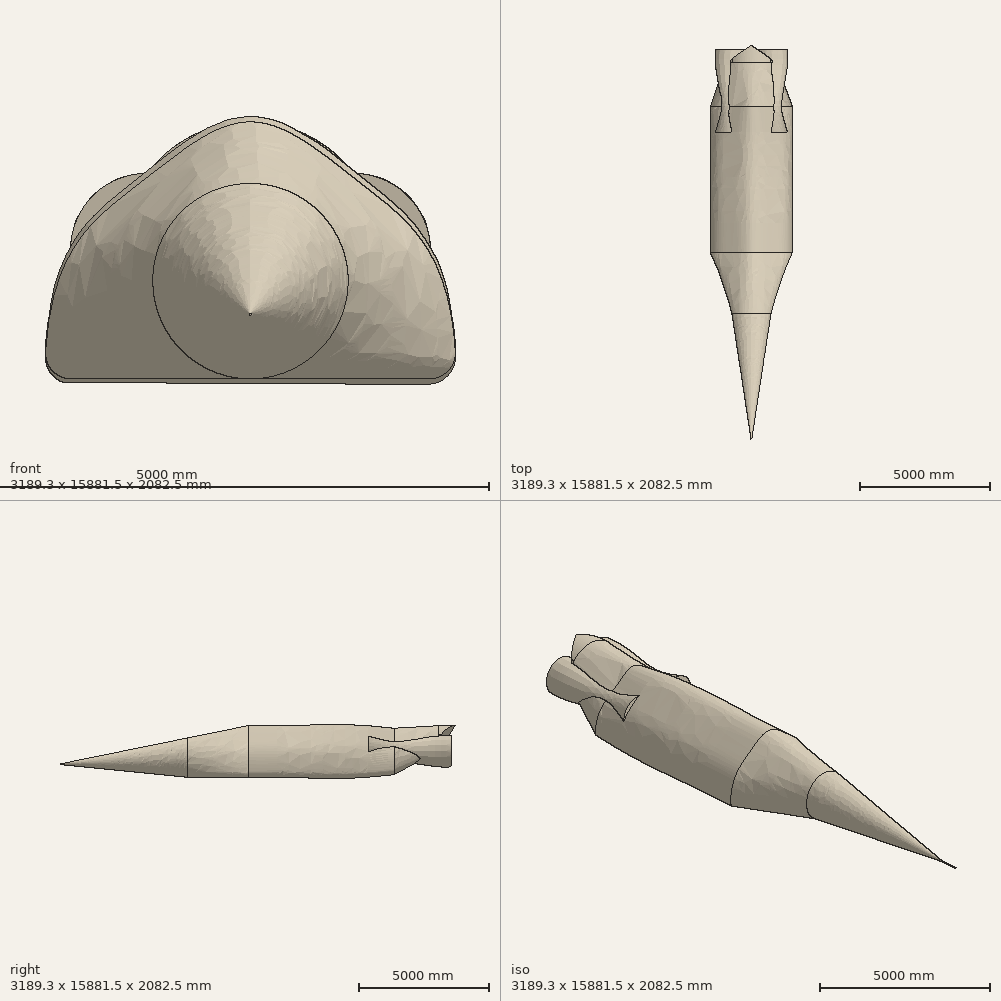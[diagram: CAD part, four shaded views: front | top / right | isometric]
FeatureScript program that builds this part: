
annotation { "Feature Type Name" : "Feature", "Feature Type Description" : "" }
export const myFeature = defineFeature(function(context is Context, id is Id, definition is map)
    precondition{}
    {
        {
            var Q0;
            Q0=qCreatedBy(makeId("Right.planeOp"),FACE);
            var sketch = newSketch(context, id + "F0", { "sketchPlane" : qUnion([Q0])});
            skLineSegment(sketch, "E0", {"start": v(0, 0) * mm, "end": v(-1750, 0) * mm});
            skLineSegment(sketch, "E1", {"start": v(-1750, 0) * mm, "end": v(-3500, 0) * mm});
            skLineSegment(sketch, "E2", {"start": v(-3500, 0) * mm, "end": v(-3500, -1000) * mm});
            skLineSegment(sketch, "E3", {"start": v(-3500, -1000) * mm, "end": v(-8500, -1000) * mm});
            skLineSegment(sketch, "E4", {"start": v(-8500, -1000) * mm, "end": v(-8500, -499.31) * mm});
            skLineSegment(sketch, "E5", {"start": v(-1151.4, 0) * mm, "end": v(-1151.4, 1000) * mm});
            skLineSegment(sketch, "E6", {"start": v(-1151.4, 1000) * mm, "end": v(-8500, -499.31) * mm});
            skLineSegment(sketch, "E7", {"start": v(-8500, -499.31) * mm, "end": v(-3500, -1000) * mm});
            skLineSegment(sketch, "E8", {"start": v(-3500, 0) * mm, "end": v(-3500, 520.82) * mm});
            skLineSegment(sketch, "E9", {"start": v(-8500, -499.31) * mm, "end": v(-8450, -499.31) * mm});
            skLineSegment(sketch, "E10", {"start": v(-8450, -499.31) * mm, "end": v(-8450, -489.1) * mm});
            skLineSegment(sketch, "E11", {"start": v(-8450, -499.31) * mm, "end": v(-8450, -504.32) * mm});
            skSolve(sketch);
        }
        {
            var Q0;
            Q0=sQuery(id+"F0.wireOp",EDGE,"E5");
            cPlane(context, id + "F1", {"entities" : qUnion([Q0]), "cplaneType" : CPlaneType.LINE_ANGLE, "offset" : 25 * mm, "angle" : 90 * degree, "oppositeDirection" : true, "width" : 150 * mm, "height" : 150 * mm});
        }
        {
            var Q0;
            Q0=qCreatedBy(id+"F1.planeOp",FACE);
            var sketch = newSketch(context, id + "F2", { "sketchPlane" : qUnion([Q0])});
            skLineSegment(sketch, "E12.top", {"start": v(-1394.2, -1000) * mm, "end": v(1394.2, -1000) * mm});
            skPoint(sketch, "E12.middle", {"position": v(0, 0) * mm});
            skFitSpline(sketch, "E13", {"points": [v(-1600, -1000) * mm, v(-848, 530) * mm, v(0, 1000) * mm, v(848, 530) * mm, v(1600, -1000) * mm], "startDerivative": vector(0, 10524.75) * mm, "endDerivative": vector(0, -10524.75) * mm});
            skArc(sketch, "E14", {"start": v(-735.27, 618.52) * mm, "mid": v(-1273.27, 435.52) * mm, "end": v(-1440.68, -107.53) * mm});
            skArc(sketch, "E15", {"start": v(1440.68, -107.53) * mm, "mid": v(1273.27, 435.52) * mm, "end": v(735.27, 618.52) * mm});
            skFitSpline(sketch, "E16.trimOffspring", {"points": [v(-1600, -1000) * mm, v(-848, 530) * mm, v(0, 1000) * mm, v(848, 530) * mm, v(1600, -1000) * mm], "startDerivative": vector(0, 10524.75) * mm, "endDerivative": vector(0, -10524.75) * mm});
            skFitSpline(sketch, "E17.trimOffspring", {"points": [v(-1600, -1000) * mm, v(-848, 530) * mm, v(0, 1000) * mm, v(848, 530) * mm, v(1600, -1000) * mm], "startDerivative": vector(0, 10524.75) * mm, "endDerivative": vector(0, -10524.75) * mm});
            skArc(sketch, "E18.filletArc", {"start": v(-1593.82, -787.83) * mm, "mid": v(-1539.85, -937.05) * mm, "end": v(-1394.2, -1000) * mm});
            skArc(sketch, "E19.filletArc", {"start": v(1394.2, -1000) * mm, "mid": v(1539.85, -937.05) * mm, "end": v(1593.82, -787.83) * mm});
            skSolve(sketch);
        }
        {
            var Q0;
            Q0=qCreatedBy(makeId("Front.planeOp"),FACE);
            var sketch = newSketch(context, id + "F3", { "sketchPlane" : qUnion([Q0])});
            skLineSegment(sketch, "E20.top", {"start": v(-1394.2, -1000) * mm, "end": v(1394.2, -1000) * mm});
            skPoint(sketch, "E20.middle", {"position": v(0, 0) * mm});
            skFitSpline(sketch, "E21", {"points": [v(-1600, -1000) * mm, v(-848, 530) * mm, v(0, 1000) * mm, v(848, 530) * mm, v(1600, -1000) * mm], "startDerivative": vector(0, 10524.75) * mm, "endDerivative": vector(0, -10524.75) * mm});
            skArc(sketch, "E22", {"start": v(-735.27, 618.52) * mm, "mid": v(-1273.27, 435.52) * mm, "end": v(-1440.68, -107.53) * mm});
            skArc(sketch, "E23", {"start": v(1440.68, -107.53) * mm, "mid": v(1273.27, 435.52) * mm, "end": v(735.27, 618.52) * mm});
            skFitSpline(sketch, "E24.trimOffspring", {"points": [v(-1600, -1000) * mm, v(-848, 530) * mm, v(0, 1000) * mm, v(848, 530) * mm, v(1600, -1000) * mm], "startDerivative": vector(0, 10524.75) * mm, "endDerivative": vector(0, -10524.75) * mm});
            skFitSpline(sketch, "E25.trimOffspring", {"points": [v(-1600, -1000) * mm, v(-848, 530) * mm, v(0, 1000) * mm, v(848, 530) * mm, v(1600, -1000) * mm], "startDerivative": vector(0, 10524.75) * mm, "endDerivative": vector(0, -10524.75) * mm});
            skArc(sketch, "E26.filletArc", {"start": v(-1593.82, -787.83) * mm, "mid": v(-1539.85, -937.05) * mm, "end": v(-1394.2, -1000) * mm});
            skArc(sketch, "E27.filletArc", {"start": v(1394.2, -1000) * mm, "mid": v(1539.85, -937.05) * mm, "end": v(1593.82, -787.83) * mm});
            skSolve(sketch);
        }
        {
            var Q0;
            Q0=qCreatedBy(makeId("Front.planeOp"),FACE);
            cPlane(context, id + "F4", {"entities" : qUnion([Q0]), "cplaneType" : CPlaneType.OFFSET, "offset" : 3500 * mm, "oppositeDirection" : true, "width" : 150 * mm, "height" : 150 * mm});
        }
        {
            var Q0;
            Q0=qCreatedBy(id+"F4.planeOp",FACE);
            var sketch = newSketch(context, id + "F5", { "sketchPlane" : qUnion([Q0])});
            skLineSegment(sketch, "E28.top", {"start": v(-1394.2, -1000) * mm, "end": v(1394.2, -1000) * mm});
            skPoint(sketch, "E28.middle", {"position": v(0, 0) * mm});
            skFitSpline(sketch, "E29", {"points": [v(-1600, -1000) * mm, v(-848, 530) * mm, v(0, 1000) * mm, v(848, 530) * mm, v(1600, -1000) * mm], "startDerivative": vector(0, 10524.75) * mm, "endDerivative": vector(0, -10524.75) * mm});
            skArc(sketch, "E30", {"start": v(-735.27, 618.52) * mm, "mid": v(-1273.27, 435.52) * mm, "end": v(-1440.68, -107.53) * mm});
            skArc(sketch, "E31", {"start": v(1440.68, -107.53) * mm, "mid": v(1273.27, 435.52) * mm, "end": v(735.27, 618.52) * mm});
            skFitSpline(sketch, "E32.trimOffspring", {"points": [v(-1600, -1000) * mm, v(-848, 530) * mm, v(0, 1000) * mm, v(848, 530) * mm, v(1600, -1000) * mm], "startDerivative": vector(0, 10524.75) * mm, "endDerivative": vector(0, -10524.75) * mm});
            skFitSpline(sketch, "E33.trimOffspring", {"points": [v(-1600, -1000) * mm, v(-848, 530) * mm, v(0, 1000) * mm, v(848, 530) * mm, v(1600, -1000) * mm], "startDerivative": vector(0, 10524.75) * mm, "endDerivative": vector(0, -10524.75) * mm});
            skArc(sketch, "E34.filletArc", {"start": v(-1593.82, -787.83) * mm, "mid": v(-1539.85, -937.05) * mm, "end": v(-1394.2, -1000) * mm});
            skArc(sketch, "E35.filletArc", {"start": v(1394.2, -1000) * mm, "mid": v(1539.85, -937.05) * mm, "end": v(1593.82, -787.83) * mm});
            skSolve(sketch);
        }
        {
            var Q0;
            Q0=qCreatedBy(makeId("Front.planeOp"),FACE);
            cPlane(context, id + "F6", {"entities" : qUnion([Q0]), "cplaneType" : CPlaneType.OFFSET, "offset" : 4500 * mm, "oppositeDirection" : true, "width" : 150 * mm, "height" : 150 * mm});
        }
        {
            var Q0;
            Q0=qCreatedBy(id+"F6.planeOp",FACE);
            var sketch = newSketch(context, id + "F7", { "sketchPlane" : qUnion([Q0])});
            skLineSegment(sketch, "E36.top", {"start": v(-1413.07, -900) * mm, "end": v(1413.07, -900) * mm});
            skPoint(sketch, "E36.middle", {"position": v(0, 0) * mm});
            skFitSpline(sketch, "E37", {"points": [v(-1600, -900) * mm, v(-784.42, 441.24) * mm, v(0, 900) * mm, v(784.42, 441.24) * mm, v(1600, -900) * mm], "startDerivative": vector(0, 9508.62) * mm, "endDerivative": vector(0, -9508.62) * mm});
            skArc(sketch, "E38", {"start": v(-719.25, 488.69) * mm, "mid": v(-1131.76, 394.84) * mm, "end": v(-1324.66, 18.33) * mm});
            skArc(sketch, "E39", {"start": v(1324.66, 18.33) * mm, "mid": v(1131.76, 394.84) * mm, "end": v(719.25, 488.69) * mm});
            skFitSpline(sketch, "E40.trimOffspring", {"points": [v(-1600, -900) * mm, v(-784.42, 441.24) * mm, v(0, 900) * mm, v(784.42, 441.24) * mm, v(1600, -900) * mm], "startDerivative": vector(0, 9508.62) * mm, "endDerivative": vector(0, -9508.62) * mm});
            skFitSpline(sketch, "E41.trimOffspring", {"points": [v(-1600, -900) * mm, v(-784.42, 441.24) * mm, v(0, 900) * mm, v(784.42, 441.24) * mm, v(1600, -900) * mm], "startDerivative": vector(0, 9508.62) * mm, "endDerivative": vector(0, -9508.62) * mm});
            skArc(sketch, "E42.filletArc", {"start": v(-1592.48, -705.43) * mm, "mid": v(-1545.4, -842.02) * mm, "end": v(-1413.07, -900) * mm});
            skArc(sketch, "E43.filletArc", {"start": v(1413.07, -900) * mm, "mid": v(1545.4, -842.02) * mm, "end": v(1592.48, -705.43) * mm});
            skLineSegment(sketch, "E44", {"start": v(-719.25, 488.69) * mm, "end": v(-1324.66, 18.33) * mm, "construction": true});
            skLineSegment(sketch, "E45", {"start": v(719.25, 488.69) * mm, "end": v(1324.66, 18.33) * mm, "construction": true});
            skSolve(sketch);
        }
        {
            var Q0;
            Q0=qCreatedBy(makeId("Front.planeOp"),FACE);
            cPlane(context, id + "F8", {"entities" : qUnion([Q0]), "cplaneType" : CPlaneType.OFFSET, "offset" : 6232.05 * mm, "oppositeDirection" : true, "width" : 150 * mm, "height" : 150 * mm});
        }
        {
            var Q0;
            Q0=qCreatedBy(id+"F8.planeOp",FACE);
            var sketch = newSketch(context, id + "F9", { "sketchPlane" : qUnion([Q0])});
            skArc(sketch, "E46", {"start": v(998.61, 52.63) * mm, "mid": v(0, 1000) * mm, "end": v(-998.61, 52.63) * mm});
            skLineSegment(sketch, "E47", {"start": v(0, 0) * mm, "end": v(-948.68, 0) * mm});
            skLineSegment(sketch, "E48", {"start": v(0, 0) * mm, "end": v(948.68, 0) * mm});
            skLineSegment(sketch, "E49", {"start": v(0, 1000) * mm, "end": v(0, 675) * mm, "construction": true});
            skLineSegment(sketch, "E50", {"start": v(0, 675) * mm, "end": v(-737.82, 675) * mm, "construction": true});
            skLineSegment(sketch, "E51", {"start": v(0, 675) * mm, "end": v(737.82, 675) * mm, "construction": true});
            skPoint(sketch, "E52.visualSharp", {"position": v(-1000, 0) * mm});
            skArc(sketch, "E52.filletArc", {"start": v(-998.61, 52.63) * mm, "mid": v(-984.96, 15.59) * mm, "end": v(-948.68, 0) * mm});
            skPoint(sketch, "E53.visualSharp", {"position": v(1000, 0) * mm});
            skArc(sketch, "E53.filletArc", {"start": v(948.68, 0) * mm, "mid": v(984.96, 15.59) * mm, "end": v(998.61, 52.63) * mm});
            skSolve(sketch);
        }
        {
            var Q0;
            Q0=makeQuery(id+"F2.imprint","IMPRINT",FACE,{"disambiguationData":[TD([[makeQuery(id+"F2.imprint","IMPRINT",EDGE,{"derivedFrom":sQuery(id+"F2.wireOp",EDGE,"E12.top")}),1.0]])]});
            var Q1;
            Q1=makeQuery(id+"F3.imprint","IMPRINT",FACE,{"disambiguationData":[TD([[makeQuery(id+"F3.imprint","IMPRINT",EDGE,{"derivedFrom":sQuery(id+"F3.wireOp",EDGE,"E20.top")}),1.0]])]});
            var Q2;
            Q2=makeQuery(id+"F5.imprint","IMPRINT",FACE,{"disambiguationData":[TD([[makeQuery(id+"F5.imprint","IMPRINT",EDGE,{"derivedFrom":sQuery(id+"F5.wireOp",EDGE,"E28.top")}),1.0]])]});
            var Q3;
            Q3=makeQuery(id+"F7.imprint","IMPRINT",FACE,{"disambiguationData":[TD([[makeQuery(id+"F7.imprint","IMPRINT",EDGE,{"derivedFrom":sQuery(id+"F7.wireOp",EDGE,"E36.top")}),1.0]])]});
            loft(context, id + "F10", {"sheetProfilesArray" : [{ "sheetProfileEntities" : qUnion([Q0]) }, { "sheetProfileEntities" : qUnion([Q1]) }, { "sheetProfileEntities" : qUnion([Q2]) }, { "sheetProfileEntities" : qUnion([Q3]) }]});
        }
        {
            var Q0;
            Q0=sQuery(id+"F7.wireOp",EDGE,"E44");
            var Q1;
            Q1=sQuery(id+"F9.wireOp",VERTEX,"E50.end");
            cPlane(context, id + "F11", {"entities" : qUnion([Q0, Q1]), "cplaneType" : CPlaneType.LINE_ANGLE, "offset" : 25 * mm, "angle" : 180 * degree, "width" : 150 * mm, "height" : 150 * mm});
        }
        {
            var Q0;
            Q0=qCreatedBy(id+"F11.planeOp",FACE);
            var sketch = newSketch(context, id + "F12", { "sketchPlane" : qUnion([Q0])});
            skLineSegment(sketch, "E54", {"start": v(-589.34, 4526.34) * mm, "end": v(-612.8, 6268.32) * mm});
            skLineSegment(sketch, "E55", {"start": v(-1354.08, 4472.19) * mm, "end": v(-612.8, 6268.32) * mm});
            skSolve(sketch);
        }
        {
            var Q0;
            Q0=sQuery(id+"F7.wireOp",EDGE,"E45");
            var Q1;
            Q1=sQuery(id+"F9.wireOp",VERTEX,"E51.end");
            cPlane(context, id + "F13", {"entities" : qUnion([Q0, Q1]), "cplaneType" : CPlaneType.LINE_ANGLE, "offset" : 25 * mm, "angle" : 0 * degree, "width" : 150 * mm, "height" : 150 * mm});
        }
        {
            var Q0;
            Q0=qCreatedBy(id+"F13.planeOp",FACE);
            var sketch = newSketch(context, id + "F14", { "sketchPlane" : qUnion([Q0])});
            skLineSegment(sketch, "E56", {"start": v(589.34, 4526.34) * mm, "end": v(612.8, 6268.32) * mm});
            skLineSegment(sketch, "E57", {"start": v(1354.08, 4472.19) * mm, "end": v(612.8, 6268.32) * mm});
            skSolve(sketch);
        }
        {
            var Q1;
            Q1=makeQuery(id+"F10.opLoft","CAP_FACE",FACE,{"disambiguationData":[OSD([makeQuery(id+"F7.imprint","IMPRINT",FACE,{"disambiguationData":[TD([[makeQuery(id+"F7.imprint","IMPRINT",EDGE,{"derivedFrom":sQuery(id+"F7.wireOp",EDGE,"E36.top")}),1.0]])]})])],"isStart":true});
            var Q2;
            Q2=makeQuery(id+"F9.imprint","IMPRINT",FACE,{"disambiguationData":[TD([[makeQuery(id+"F9.imprint","IMPRINT",EDGE,{"derivedFrom":sQuery(id+"F9.wireOp",EDGE,"E46")}),1.0]])]});
            var Q3;
            Q3=sQuery(id+"F12.wireOp",EDGE,"E54");
            var Q4;
            Q4=sQuery(id+"F14.wireOp",EDGE,"E56");
            loft(context, id + "F15", {"operationType" : NewBodyOperationType.ADD, "addGuides" : true, "sheetProfilesArray" : [{ "sheetProfileEntities" : qUnion([Q1]) }, { "sheetProfileEntities" : qUnion([Q2]) }], "guidesArray" : [{ "guideEntities" : qUnion([Q3]), "guideDerivativeType" : LoftGuideDerivativeType.DEFAULT, "guideDerivativeMagnitude" : 1 }, { "guideEntities" : qUnion([Q4]), "guideDerivativeType" : LoftGuideDerivativeType.DEFAULT, "guideDerivativeMagnitude" : 1 }]});
        }
        {
            var Q0;
            Q0=makeQuery(id+"F15.opLoft","CAP_FACE",FACE,{"disambiguationData":[OSD([makeQuery(id+"F9.imprint","IMPRINT",FACE,{"disambiguationData":[TD([[makeQuery(id+"F9.imprint","IMPRINT",EDGE,{"derivedFrom":sQuery(id+"F9.wireOp",EDGE,"E46")}),1.0]])]})])],"isStart":true});
            extrude(context, id + "F16", {"entities" : qUnion([Q0]), "operationType" : NewBodyOperationType.ADD, "depth" : 649.4 * mm, "offsetDistance" : 25 * mm});
        }
        {
            var Q0;
            Q0=qCreatedBy(makeId("Right.planeOp"),FACE);
            var sketch = newSketch(context, id + "F17", { "sketchPlane" : qUnion([Q0])});
            skLineSegment(sketch, "E58", {"start": v(0, 0) * mm, "end": v(4500, 0) * mm});
            skLineSegment(sketch, "E59", {"start": v(4500, 0) * mm, "end": v(6232.05, 0) * mm});
            skLineSegment(sketch, "E60", {"start": v(4500, 0) * mm, "end": v(4500, 1000) * mm});
            skLineSegment(sketch, "E61", {"start": v(4500, 1000) * mm, "end": v(6881.46, 1000) * mm});
            skLineSegment(sketch, "E62", {"start": v(6881.46, 1000) * mm, "end": v(6881.46, -1000) * mm});
            skLineSegment(sketch, "E63", {"start": v(6881.46, 1000) * mm, "end": v(6232.05, 0) * mm});
            skLineSegment(sketch, "E64", {"start": v(6232.05, 0) * mm, "end": v(5582.64, -1000) * mm});
            skLineSegment(sketch, "E65", {"start": v(5582.64, -1000) * mm, "end": v(6881.46, -1000) * mm});
            skSolve(sketch);
        }
        {
            var Q0;
            Q0=makeQuery(id+"F17.imprint","IMPRINT",FACE,{"disambiguationData":[TD([[makeQuery(id+"F17.imprint","IMPRINT",EDGE,{"derivedFrom":sQuery(id+"F17.wireOp",EDGE,"E62")}),-1.0]])]});
            var Q1;
            Q1=sQuery(id+"F17.wireOp",EDGE,"E61");
            revolve(context, id + "F18", {"operationType" : NewBodyOperationType.REMOVE, "entities" : qUnion([Q0]), "axis" : qUnion([Q1]), "revolveType" : RevolveType.SYMMETRIC, "oppositeDirection" : true, "angle" : 182 * degree});
        }
        {
            var Q0;
            Q0=qCreatedBy(id+"F1.planeOp",FACE);
            var sketch = newSketch(context, id + "F19", { "sketchPlane" : qUnion([Q0])});
            skLineSegment(sketch, "E66.top", {"start": v(-1394.2, -1000) * mm, "end": v(1394.2, -1000) * mm});
            skPoint(sketch, "E66.middle", {"position": v(0, 0) * mm});
            skFitSpline(sketch, "E67", {"points": [v(-1600, -1000) * mm, v(-848, 530) * mm, v(0, 1000) * mm, v(848, 530) * mm, v(1600, -1000) * mm], "startDerivative": vector(0, 10524.75) * mm, "endDerivative": vector(0, -10524.75) * mm});
            skArc(sketch, "E68.filletArc", {"start": v(-1593.82, -787.83) * mm, "mid": v(-1539.85, -937.05) * mm, "end": v(-1394.2, -1000) * mm});
            skArc(sketch, "E69.filletArc", {"start": v(1394.2, -1000) * mm, "mid": v(1539.85, -937.05) * mm, "end": v(1593.82, -787.83) * mm});
            skLineSegment(sketch, "E70", {"start": v(-1593.82, -787.83) * mm, "end": v(-1394.2, -1000) * mm, "construction": true});
            skLineSegment(sketch, "E71", {"start": v(1593.82, -787.83) * mm, "end": v(1394.2, -1000) * mm, "construction": true});
            skSolve(sketch);
        }
        {
            var Q0;
            Q0=qCreatedBy(makeId("Front.planeOp"),FACE);
            cPlane(context, id + "F20", {"entities" : qUnion([Q0]), "cplaneType" : CPlaneType.OFFSET, "offset" : 3500 * mm, "width" : 150 * mm, "height" : 150 * mm});
        }
        {
            var Q0;
            Q0=qCreatedBy(id+"F20.planeOp",FACE);
            var sketch = newSketch(context, id + "F21", { "sketchPlane" : qUnion([Q0])});
            skCircle(sketch, "E72", {"center": v(0, -239.59) * mm, "radius": 760.41 * mm});
            skLineSegment(sketch, "E73", {"start": v(0, -1000) * mm, "end": v(0, -800) * mm, "construction": true});
            skLineSegment(sketch, "E74", {"start": v(0, -800) * mm, "end": v(-513.97, -800) * mm, "construction": true});
            skLineSegment(sketch, "E75", {"start": v(0, -800) * mm, "end": v(513.97, -800) * mm, "construction": true});
            skSolve(sketch);
        }
        {
            var Q0;
            Q0=qCreatedBy(makeId("Front.planeOp"),FACE);
            cPlane(context, id + "F22", {"entities" : qUnion([Q0]), "cplaneType" : CPlaneType.OFFSET, "offset" : 8450 * mm, "width" : 150 * mm, "height" : 150 * mm});
        }
        {
            var Q0;
            Q0=qCreatedBy(id+"F22.planeOp",FACE);
            var sketch = newSketch(context, id + "F23", { "sketchPlane" : qUnion([Q0])});
            skCircle(sketch, "E76", {"center": v(0, -496.71) * mm, "radius": 7.6 * mm});
            skSolve(sketch);
        }
        {
            var Q0;
            Q0=sQuery(id+"F19.wireOp",EDGE,"E70");
            var Q1;
            Q1=sQuery(id+"F21.wireOp",VERTEX,"E74.end");
            cPlane(context, id + "F24", {"entities" : qUnion([Q0, Q1]), "cplaneType" : CPlaneType.LINE_ANGLE, "offset" : 25 * mm, "angle" : 0 * degree, "width" : 150 * mm, "height" : 150 * mm});
        }
        {
            var Q0;
            Q0=qCreatedBy(id+"F24.planeOp",FACE);
            var sketch = newSketch(context, id + "F25", { "sketchPlane" : qUnion([Q0])});
            skLineSegment(sketch, "E77", {"start": v(3032.27, -230.44) * mm, "end": v(558.11, 518.4) * mm});
            skLineSegment(sketch, "E78", {"start": v(3032.27, -230.44) * mm, "end": v(558.11, 227.09) * mm});
            skSolve(sketch);
        }
        {
            var Q0;
            Q0=sQuery(id+"F19.wireOp",EDGE,"E71");
            var Q1;
            Q1=sQuery(id+"F21.wireOp",VERTEX,"E75.end");
            cPlane(context, id + "F26", {"entities" : qUnion([Q0, Q1]), "cplaneType" : CPlaneType.LINE_ANGLE, "offset" : 25 * mm, "angle" : 180 * degree, "width" : 150 * mm, "height" : 150 * mm});
        }
        {
            var Q0;
            Q0=qCreatedBy(id+"F26.planeOp",FACE);
            var sketch = newSketch(context, id + "F27", { "sketchPlane" : qUnion([Q0])});
            skLineSegment(sketch, "E79", {"start": v(-3032.27, -230.44) * mm, "end": v(-558.11, 518.4) * mm});
            skLineSegment(sketch, "E80", {"start": v(-3032.27, -230.44) * mm, "end": v(-558.11, 227.09) * mm});
            skSolve(sketch);
        }
        {
            var Q1;
            Q1=makeQuery(id+"F19.imprint","IMPRINT",FACE,{"disambiguationData":[TD([[makeQuery(id+"F19.imprint","IMPRINT",EDGE,{"derivedFrom":sQuery(id+"F19.wireOp",EDGE,"E66.top")}),1.0]])]});
            var Q2;
            Q2=makeQuery(id+"F21.imprint","IMPRINT",FACE,{"disambiguationData":[TD([[makeQuery(id+"F21.imprint","IMPRINT",EDGE,{"derivedFrom":sQuery(id+"F21.wireOp",EDGE,"E72")}),1.0]])]});
            var Q3;
            Q3=sQuery(id+"F25.wireOp",EDGE,"E77");
            var Q4;
            Q4=sQuery(id+"F27.wireOp",EDGE,"E79");
            loft(context, id + "F28", {"operationType" : NewBodyOperationType.ADD, "addGuides" : true, "sheetProfilesArray" : [{ "sheetProfileEntities" : qUnion([Q1]) }, { "sheetProfileEntities" : qUnion([Q2]) }], "guidesArray" : [{ "guideEntities" : qUnion([Q3]), "guideDerivativeType" : LoftGuideDerivativeType.DEFAULT, "guideDerivativeMagnitude" : 1 }, { "guideEntities" : qUnion([Q4]), "guideDerivativeType" : LoftGuideDerivativeType.DEFAULT, "guideDerivativeMagnitude" : 1 }]});
        }
        {
            var Q1;
            Q1=makeQuery(id+"F28.opLoft","CAP_FACE",FACE,{"disambiguationData":[OSD([makeQuery(id+"F21.imprint","IMPRINT",FACE,{"disambiguationData":[TD([[makeQuery(id+"F21.imprint","IMPRINT",EDGE,{"derivedFrom":sQuery(id+"F21.wireOp",EDGE,"E72")}),1.0]])]})])],"isStart":true});
            var Q2;
            Q2=makeQuery(id+"F23.imprint","IMPRINT",FACE,{"disambiguationData":[TD([[makeQuery(id+"F23.imprint","IMPRINT",EDGE,{"derivedFrom":sQuery(id+"F23.wireOp",EDGE,"E76")}),1.0]])]});
            loft(context, id + "F29", {"operationType" : NewBodyOperationType.ADD, "sheetProfilesArray" : [{ "sheetProfileEntities" : qUnion([Q1]) }, { "sheetProfileEntities" : qUnion([Q2]) }]});
        }
        {
            var Q0;
            Q0=makeQuery(id+"F29.opLoft","CAP_FACE",FACE,{"disambiguationData":[OSD([makeQuery(id+"F23.imprint","IMPRINT",FACE,{"disambiguationData":[TD([[makeQuery(id+"F23.imprint","IMPRINT",EDGE,{"derivedFrom":sQuery(id+"F23.wireOp",EDGE,"E76")}),1.0]])]})])],"isStart":true});
            extrude(context, id + "F30", {"entities" : qUnion([Q0]), "operationType" : NewBodyOperationType.ADD, "depth" : 550 * mm, "offsetDistance" : 25 * mm});
        }
        {
            var Q0;
            Q0=qCreatedBy(makeId("Front.planeOp"),FACE);
            cPlane(context, id + "F31", {"entities" : qUnion([Q0]), "cplaneType" : CPlaneType.OFFSET, "offset" : 3500 * mm, "oppositeDirection" : true, "width" : 150 * mm, "height" : 150 * mm});
        }
        {
            var Q0;
            Q0=qCreatedBy(id+"F31.planeOp",FACE);
            var sketch = newSketch(context, id + "F32", { "sketchPlane" : qUnion([Q0])});
            skCircle(sketch, "E81", {"center": v(-800, 0) * mm, "radius": 600 * mm});
            skCircle(sketch, "E82", {"center": v(800, 0) * mm, "radius": 600 * mm});
            skSolve(sketch);
        }
        {
            var Q0;
            Q0=qCreatedBy(makeId("Front.planeOp"),FACE);
            cPlane(context, id + "F33", {"entities" : qUnion([Q0]), "cplaneType" : CPlaneType.OFFSET, "offset" : 4500 * mm, "oppositeDirection" : true, "width" : 150 * mm, "height" : 150 * mm});
        }
        {
            var Q0;
            Q0=qCreatedBy(id+"F33.planeOp",FACE);
            var sketch = newSketch(context, id + "F34", { "sketchPlane" : qUnion([Q0])});
            skCircle(sketch, "E83", {"center": v(-800, 0) * mm, "radius": 400 * mm});
            skCircle(sketch, "E84", {"center": v(800, 0) * mm, "radius": 400 * mm});
            skSolve(sketch);
        }
        {
            var Q0;
            Q0=qCreatedBy(makeId("Front.planeOp"),FACE);
            cPlane(context, id + "F35", {"entities" : qUnion([Q0]), "cplaneType" : CPlaneType.OFFSET, "offset" : 6232.05 * mm, "oppositeDirection" : true, "width" : 150 * mm, "height" : 150 * mm});
        }
        {
            var Q0;
            Q0=qCreatedBy(id+"F35.planeOp",FACE);
            var sketch = newSketch(context, id + "F36", { "sketchPlane" : qUnion([Q0])});
            skCircle(sketch, "E85", {"center": v(-800, 0) * mm, "radius": 600 * mm});
            skCircle(sketch, "E86", {"center": v(800, 0) * mm, "radius": 600 * mm});
            skSolve(sketch);
        }
        {
            var Q0;
            Q0=qCreatedBy(makeId("Front.planeOp"),FACE);
            cPlane(context, id + "F37", {"entities" : qUnion([Q0]), "cplaneType" : CPlaneType.OFFSET, "offset" : 6732.05 * mm, "oppositeDirection" : true, "width" : 150 * mm, "height" : 150 * mm});
        }
        {
            var Q0;
            Q0=qCreatedBy(id+"F37.planeOp",FACE);
            var sketch = newSketch(context, id + "F38", { "sketchPlane" : qUnion([Q0])});
            skCircle(sketch, "E87", {"center": v(-800, 0) * mm, "radius": 600 * mm});
            skCircle(sketch, "E88", {"center": v(800, 0) * mm, "radius": 600 * mm});
            skSolve(sketch);
        }
        {
            var Q0;
            Q0=makeQuery(id+"F32.imprint","IMPRINT",FACE,{"disambiguationData":[TD([[makeQuery(id+"F32.imprint","IMPRINT",EDGE,{"derivedFrom":sQuery(id+"F32.wireOp",EDGE,"E81")}),1.0]])]});
            var Q1;
            Q1=makeQuery(id+"F34.imprint","IMPRINT",FACE,{"disambiguationData":[TD([[makeQuery(id+"F34.imprint","IMPRINT",EDGE,{"derivedFrom":sQuery(id+"F34.wireOp",EDGE,"E83")}),1.0]])]});
            var Q2;
            Q2=makeQuery(id+"F36.imprint","IMPRINT",FACE,{"disambiguationData":[TD([[makeQuery(id+"F36.imprint","IMPRINT",EDGE,{"derivedFrom":sQuery(id+"F36.wireOp",EDGE,"E85")}),1.0]])]});
            var Q3;
            Q3=makeQuery(id+"F38.imprint","IMPRINT",FACE,{"disambiguationData":[TD([[makeQuery(id+"F38.imprint","IMPRINT",EDGE,{"derivedFrom":sQuery(id+"F38.wireOp",EDGE,"E87")}),1.0]])]});
            loft(context, id + "F39", {"sheetProfilesArray" : [{ "sheetProfileEntities" : qUnion([Q0]) }, { "sheetProfileEntities" : qUnion([Q1]) }, { "sheetProfileEntities" : qUnion([Q2]) }, { "sheetProfileEntities" : qUnion([Q3]) }]});
        }
        {
            var Q0;
            Q0=makeQuery(id+"F32.imprint","IMPRINT",FACE,{"disambiguationData":[TD([[makeQuery(id+"F32.imprint","IMPRINT",EDGE,{"derivedFrom":sQuery(id+"F32.wireOp",EDGE,"E82")}),1.0]])]});
            var Q1;
            Q1=makeQuery(id+"F34.imprint","IMPRINT",FACE,{"disambiguationData":[TD([[makeQuery(id+"F34.imprint","IMPRINT",EDGE,{"derivedFrom":sQuery(id+"F34.wireOp",EDGE,"E84")}),1.0]])]});
            var Q2;
            Q2=makeQuery(id+"F36.imprint","IMPRINT",FACE,{"disambiguationData":[TD([[makeQuery(id+"F36.imprint","IMPRINT",EDGE,{"derivedFrom":sQuery(id+"F36.wireOp",EDGE,"E86")}),1.0]])]});
            var Q3;
            Q3=makeQuery(id+"F38.imprint","IMPRINT",FACE,{"disambiguationData":[TD([[makeQuery(id+"F38.imprint","IMPRINT",EDGE,{"derivedFrom":sQuery(id+"F38.wireOp",EDGE,"E88")}),1.0]])]});
            loft(context, id + "F40", {"sheetProfilesArray" : [{ "sheetProfileEntities" : qUnion([Q0]) }, { "sheetProfileEntities" : qUnion([Q1]) }, { "sheetProfileEntities" : qUnion([Q2]) }, { "sheetProfileEntities" : qUnion([Q3]) }]});
        }
    });
